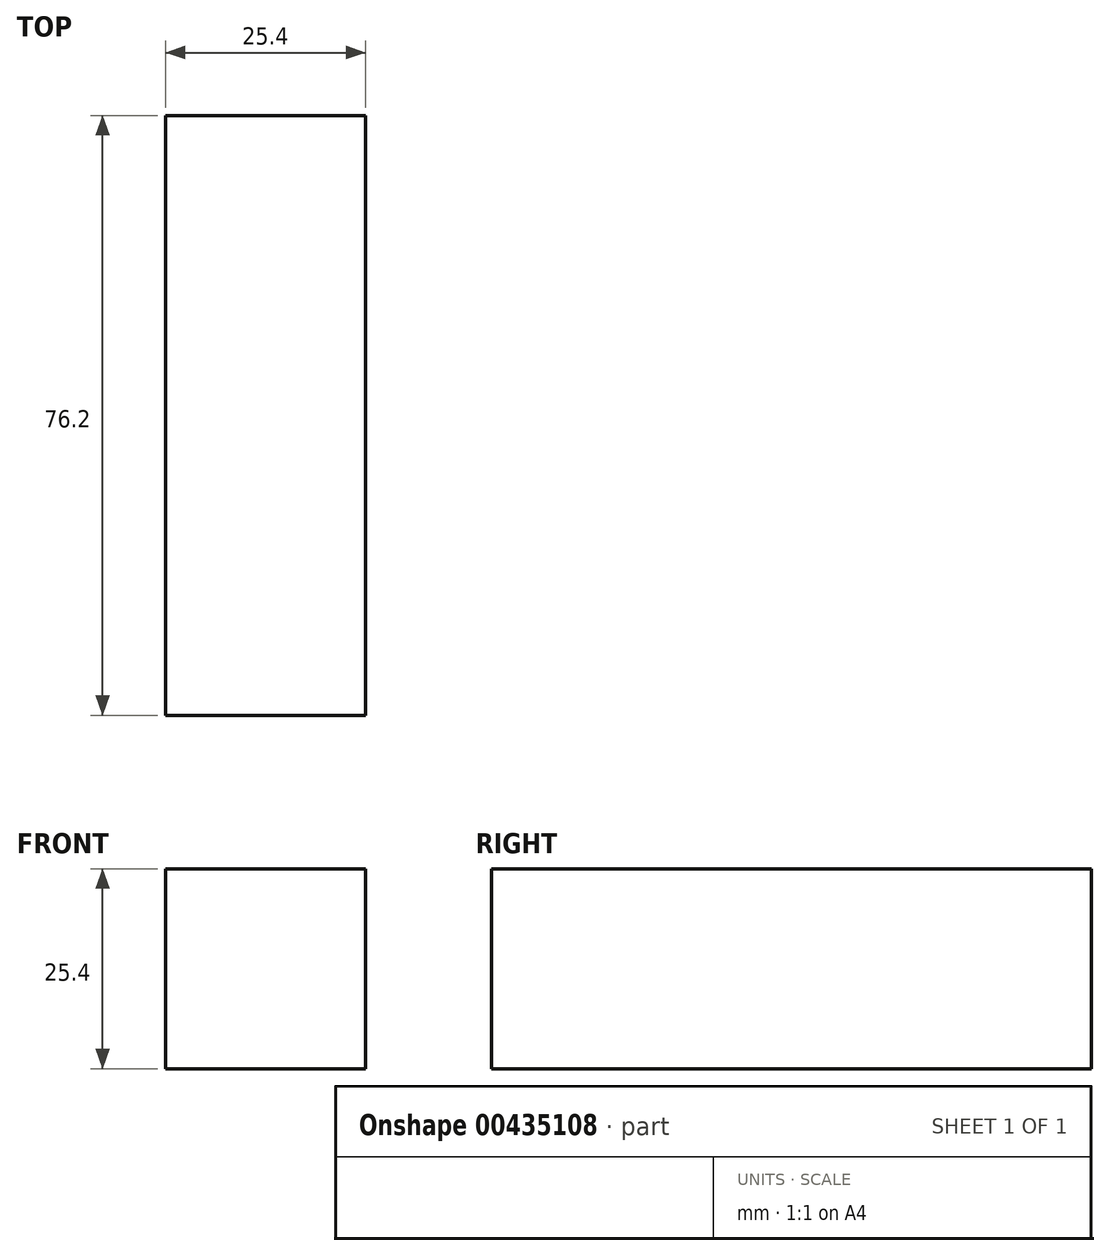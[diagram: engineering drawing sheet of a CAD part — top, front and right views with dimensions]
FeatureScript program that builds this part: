
annotation { "Feature Type Name" : "Feature", "Feature Type Description" : "" }
export const myFeature = defineFeature(function(context is Context, id is Id, definition is map)
    precondition{}
    {
        {
            var Q0;
            Q0=qCreatedBy(makeId("Front.planeOp"),FACE);
            var sketch = newSketch(context, id + "F0", { "sketchPlane" : qUnion([Q0])});
            skLineSegment(sketch, "E0.bottom", {"start": v(-30.23, 29.05) * mm, "end": v(-4.83, 29.05) * mm});
            skLineSegment(sketch, "E0.top", {"start": v(-30.23, 3.65) * mm, "end": v(-4.83, 3.65) * mm});
            skLineSegment(sketch, "E0.left", {"start": v(-30.23, 29.05) * mm, "end": v(-30.23, 3.65) * mm});
            skLineSegment(sketch, "E0.right", {"start": v(-4.83, 29.05) * mm, "end": v(-4.83, 3.65) * mm});
            skSolve(sketch);
        }
        {
            var Q0;
            Q0 = qSketchRegion(id + "F0", true);
            extrude(context, id + "F1", {"entities" : qUnion([Q0]), "depth" : 76.2 * mm});
        }
    });
